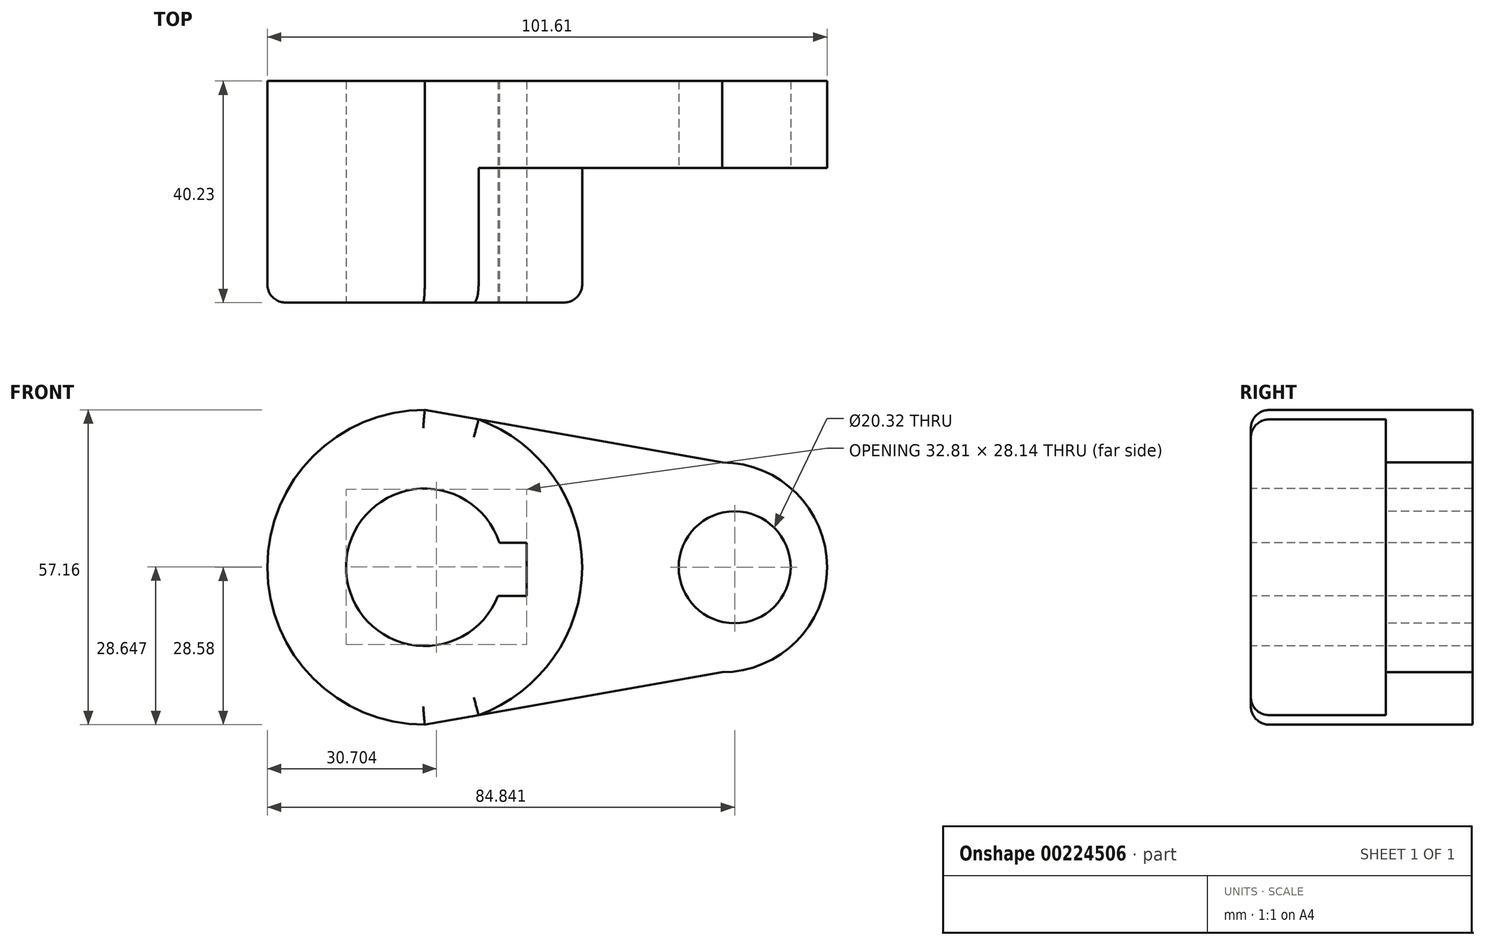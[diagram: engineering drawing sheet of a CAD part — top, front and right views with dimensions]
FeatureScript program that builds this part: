
annotation { "Feature Type Name" : "Feature", "Feature Type Description" : "" }
export const myFeature = defineFeature(function(context is Context, id is Id, definition is map)
    precondition{}
    {
        {
            var Q0;
            Q0=qCreatedBy(makeId("Front.planeOp"),FACE);
            var sketch = newSketch(context, id + "F0", { "sketchPlane" : qUnion([Q0])});
            skArc(sketch, "E0", {"start": v(9.78, 26.85) * mm, "mid": v(-28.58, 0) * mm, "end": v(9.78, -26.85) * mm});
            skArc(sketch, "E1", {"start": v(53.97, -19.05) * mm, "mid": v(73.02, 0) * mm, "end": v(53.97, 19.05) * mm});
            skLineSegment(sketch, "E2", {"start": v(0, 28.57) * mm, "end": v(53.97, 19.05) * mm});
            skLineSegment(sketch, "E3", {"start": v(0, -28.57) * mm, "end": v(53.98, -19.05) * mm});
            skSolve(sketch);
        }
        {
            var Q0;
            {var subQ3=sQuery(id+"F0.wireOp",EDGE,"E1");Q0=makeQuery(id+"F0.imprint","IMPRINT",FACE,{"disambiguationData":[TD([[makeQuery(id+"F0.imprint","IMPRINT",EDGE,{"derivedFrom":subQ3}),1.0]])]});}
            extrude(context, id + "F1", {"entities" : qUnion([Q0]), "oppositeDirection" : true, "depth" : 15.77 * mm});
        }
        {
            var Q0;
            Q0=makeQuery(id+"F1.opExtrude","CAP_FACE",FACE,{"disambiguationData":[OSD([sQuery(id+"F0.wireOp",EDGE,"E0"),sQuery(id+"F0.wireOp",EDGE,"E1"),sQuery(id+"F0.wireOp",EDGE,"E2"),sQuery(id+"F0.wireOp",EDGE,"E3")])],"isStart":true});
            var sketch = newSketch(context, id + "F2", { "sketchPlane" : qUnion([Q0])});
            skCircle(sketch, "E4", {"center": v(0, 0) * mm, "radius": 28.58 * mm});
            skSolve(sketch);
        }
        {
            var Q0;
            {var subQ0=sQuery(id+"F2.wireOp",EDGE,"E4");var subQ1=makeQuery(id+"F1.opExtrude","CAP_EDGE",EDGE,{"disambiguationData":[OSD([sQuery(id+"F0.wireOp",EDGE,"E2")])],"isStart":true});var subQ2=makeQuery(id+"F2.imprint","INTERSECT",VERTEX,{"disambiguationData":[OD(0.0)],"derivedFrom":[subQ1,subQ0]});Q0=makeQuery(id+"F2.imprint","IMPRINT",FACE,{"disambiguationData":[TD([[makeQuery(id+"F2.imprint","IMPRINT",EDGE,{"disambiguationData":[TD([[subQ2,-1.0]])],"derivedFrom":subQ0}),1.0]])]});}
            extrude(context, id + "F3", {"entities" : qUnion([Q0]), "operationType" : NewBodyOperationType.ADD, "depth" : 24.46 * mm});
        }
        {
            var Q0;
            {var subQ0=sQuery(id+"F2.wireOp",EDGE,"E4");Q0=makeQuery(id+"F3.opExtrude","CAP_EDGE",EDGE,{"disambiguationData":[OSD([subQ0]),TDD([makeQuery(id+"F2.imprint","IMPRINT",EDGE,{"disambiguationData":[TD([[makeQuery(id+"F2.imprint","INTERSECT",VERTEX,{"disambiguationData":[OD(0.0)],"derivedFrom":[makeQuery(id+"F1.opExtrude","CAP_EDGE",EDGE,{"disambiguationData":[OSD([sQuery(id+"F0.wireOp",EDGE,"E2")])],"isStart":true}),subQ0]}),-1.0]])],"derivedFrom":subQ0})])],"isStart":false});}
            var Q1;
            {var subQ0=sQuery(id+"F2.wireOp",EDGE,"E4");Q1=makeQuery(id+"F3.opExtrude","CAP_EDGE",EDGE,{"disambiguationData":[OSD([subQ0]),TDD([makeQuery(id+"F2.imprint","IMPRINT",EDGE,{"disambiguationData":[TD([[makeQuery(id+"F2.imprint","INTERSECT",VERTEX,{"disambiguationData":[OD(1.0)],"derivedFrom":[makeQuery(id+"F1.opExtrude","CAP_EDGE",EDGE,{"disambiguationData":[OSD([sQuery(id+"F0.wireOp",EDGE,"E2")])],"isStart":true}),subQ0]}),1.0]])],"derivedFrom":subQ0})])],"isStart":false});}
            var Q2;
            Q2=makeQuery(id+"F3.opExtrude","CAP_EDGE",EDGE,{"disambiguationData":[OSD([sQuery(id+"F0.wireOp",EDGE,"E3")])],"isStart":false});
            var Q3;
            Q3=makeQuery(id+"F3.opExtrude","CAP_EDGE",EDGE,{"disambiguationData":[OSD([sQuery(id+"F0.wireOp",EDGE,"E2")])],"isStart":false});
            fillet(context, id + "F4", {"entities" : qUnion([Q0, Q1, Q2, Q3]), "radius" : 3.3 * mm, "tangentPropagation" : true, "allowEdgeOverflow" : false});
        }
        {
            var Q0;
            Q0=makeQuery(id+"F3.opExtrude","CAP_FACE",FACE,{"disambiguationData":[OSD([sQuery(id+"F0.wireOp",EDGE,"E2"),sQuery(id+"F0.wireOp",EDGE,"E3"),sQuery(id+"F2.wireOp",EDGE,"E4")])],"isStart":false});
            var sketch = newSketch(context, id + "F5", { "sketchPlane" : qUnion([Q0])});
            skArc(sketch, "E5", {"start": v(13.57, 4.46) * mm, "mid": v(-14.28, 0.4) * mm, "end": v(13.3, -5.2) * mm});
            skLineSegment(sketch, "E6", {"start": v(18.53, 4.46) * mm, "end": v(13.57, 4.46) * mm});
            skLineSegment(sketch, "E7", {"start": v(18.53, -5.2) * mm, "end": v(13.3, -5.2) * mm});
            skLineSegment(sketch, "E8", {"start": v(18.53, 4.46) * mm, "end": v(18.53, -5.2) * mm});
            skSolve(sketch);
        }
        {
            var Q0;
            Q0=makeQuery(id+"F5.imprint","IMPRINT",FACE,{"disambiguationData":[TD([[makeQuery(id+"F5.imprint","IMPRINT",EDGE,{"derivedFrom":sQuery(id+"F5.wireOp",EDGE,"E5")}),1.0]])]});
            extrude(context, id + "F6", {"entities" : qUnion([Q0]), "operationType" : NewBodyOperationType.REMOVE, "endBound" : BoundingType.THROUGH_ALL, "oppositeDirection" : true, "depth" : 25.4 * mm});
        }
        {
            var Q0;
            Q0=makeQuery(id+"F1.opExtrude","CAP_FACE",FACE,{"disambiguationData":[OSD([sQuery(id+"F0.wireOp",EDGE,"E0"),sQuery(id+"F0.wireOp",EDGE,"E1"),sQuery(id+"F0.wireOp",EDGE,"E2"),sQuery(id+"F0.wireOp",EDGE,"E3")])],"isStart":true});
            var sketch = newSketch(context, id + "F7", { "sketchPlane" : qUnion([Q0])});
            skCircle(sketch, "E9", {"center": v(56.26, 0) * mm, "radius": 10.16 * mm});
            skPoint(sketch, "E9.centerSnap0", {"position": v(73.02, 0) * mm});
            skSolve(sketch);
        }
        {
            var Q0;
            Q0=makeQuery(id+"F7.imprint","IMPRINT",FACE,{"disambiguationData":[TD([[makeQuery(id+"F7.imprint","IMPRINT",EDGE,{"derivedFrom":sQuery(id+"F7.wireOp",EDGE,"E9")}),1.0]])]});
            extrude(context, id + "F8", {"entities" : qUnion([Q0]), "operationType" : NewBodyOperationType.REMOVE, "endBound" : BoundingType.THROUGH_ALL, "oppositeDirection" : true, "depth" : 25.4 * mm});
        }
    });
